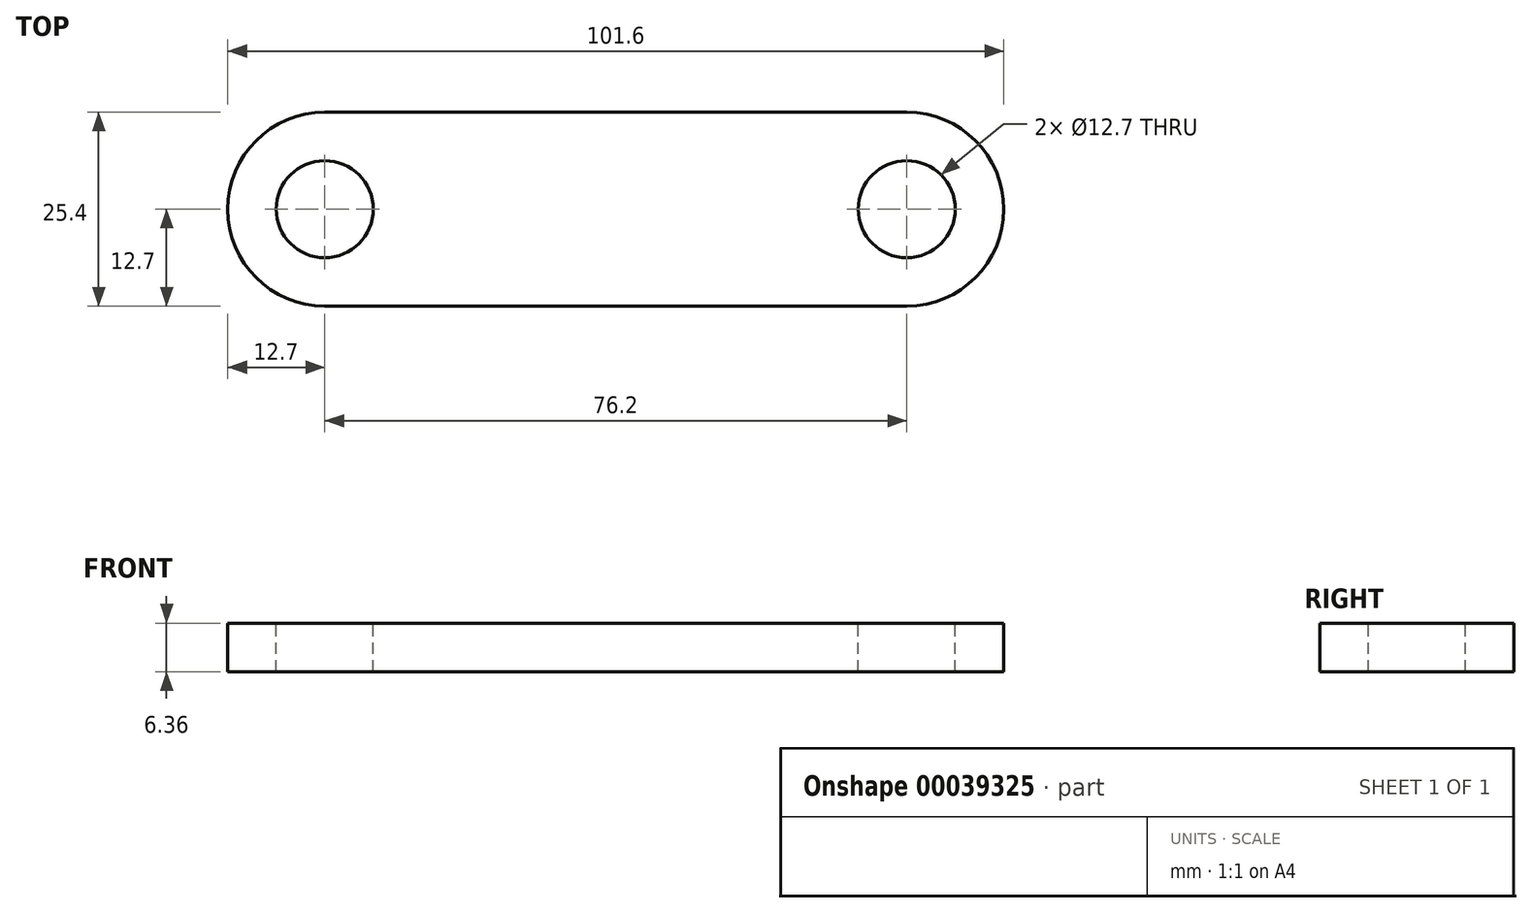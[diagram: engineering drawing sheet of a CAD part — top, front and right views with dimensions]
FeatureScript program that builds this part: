
annotation { "Feature Type Name" : "Feature", "Feature Type Description" : "" }
export const myFeature = defineFeature(function(context is Context, id is Id, definition is map)
    precondition{}
    {
        {
            var Q0;
            Q0=qCreatedBy(makeId("Top.planeOp"),FACE);
            var sketch = newSketch(context, id + "F0", { "sketchPlane" : qUnion([Q0])});
            skLineSegment(sketch, "E0.rect.bottom", {"start": v(50.8, 12.7) * mm, "end": v(-50.8, 12.7) * mm});
            skLineSegment(sketch, "E0.rect.top", {"start": v(50.8, -12.7) * mm, "end": v(-50.8, -12.7) * mm});
            skLineSegment(sketch, "E0.rect.left", {"start": v(50.8, 12.7) * mm, "end": v(50.8, -12.7) * mm});
            skLineSegment(sketch, "E0.rect.right", {"start": v(-50.8, 12.7) * mm, "end": v(-50.8, -12.7) * mm});
            skPoint(sketch, "E0.rect.middle", {"position": v(0, 0) * mm});
            skSolve(sketch);
        }
        {
            var Q0;
            Q0=makeQuery(id+"F0.imprint","IMPRINT",FACE,{"disambiguationData":[TD([[makeQuery(id+"F0.imprint","IMPRINT",EDGE,{"derivedFrom":sQuery(id+"F0.wireOp",EDGE,"E0.rect.bottom")}),1.0]])]});
            extrude(context, id + "F1", {"entities" : qUnion([Q0]), "depth" : 3.17 * mm, "hasSecondDirection" : true, "secondDirectionOppositeDirection" : true, "secondDirectionDepth" : 3.17 * mm});
        }
        {
            var Q0;
            Q0=makeQuery(id+"F1.opExtrude","CAP_FACE",FACE,{"disambiguationData":[OSD([sQuery(id+"F0.wireOp",EDGE,"E0.rect.bottom"),sQuery(id+"F0.wireOp",EDGE,"E0.rect.top"),sQuery(id+"F0.wireOp",EDGE,"E0.rect.left"),sQuery(id+"F0.wireOp",EDGE,"E0.rect.right")])],"isStart":false});
            var sketch = newSketch(context, id + "F2", { "sketchPlane" : qUnion([Q0])});
            skCircle(sketch, "E1", {"center": v(38.1, 0) * mm, "radius": 6.35 * mm});
            skLineSegment(sketch, "E2", {"start": v(0, 12.7) * mm, "end": v(0, -12.7) * mm, "construction": true});
            skCircle(sketch, "E3.MirrorC", {"center": v(-38.1, 0) * mm, "radius": 6.35 * mm});
            skSolve(sketch);
        }
        {
            var Q0;
            Q0 = qSketchRegion(id + "F2", true);
            extrude(context, id + "F3", {"entities" : qUnion([Q0]), "operationType" : NewBodyOperationType.REMOVE, "endBound" : BoundingType.THROUGH_ALL, "oppositeDirection" : true, "depth" : 25.4 * mm});
        }
        {
            var Q0;
            Q0 = qSketchRegion(id + "F2", true);
            extrude(context, id + "F4", {"entities" : qUnion([Q0]), "operationType" : NewBodyOperationType.REMOVE, "endBound" : BoundingType.THROUGH_ALL, "oppositeDirection" : true, "depth" : 25.4 * mm});
        }
        {
            var Q0;
            Q0=makeQuery(id+"F1.opExtrude","SWEPT_EDGE",EDGE,{"disambiguationData":[OSD([sQuery(id+"F0.wireOp",EDGE,"E0.rect.top"),sQuery(id+"F0.wireOp",EDGE,"E0.rect.left")])]});
            var Q1;
            Q1=makeQuery(id+"F1.opExtrude","SWEPT_EDGE",EDGE,{"disambiguationData":[OSD([sQuery(id+"F0.wireOp",EDGE,"E0.rect.top"),sQuery(id+"F0.wireOp",EDGE,"E0.rect.right")])]});
            var Q2;
            Q2=makeQuery(id+"F1.opExtrude","SWEPT_EDGE",EDGE,{"disambiguationData":[OSD([sQuery(id+"F0.wireOp",EDGE,"E0.rect.bottom"),sQuery(id+"F0.wireOp",EDGE,"E0.rect.left")])]});
            var Q3;
            Q3=makeQuery(id+"F1.opExtrude","SWEPT_EDGE",EDGE,{"disambiguationData":[OSD([sQuery(id+"F0.wireOp",EDGE,"E0.rect.bottom"),sQuery(id+"F0.wireOp",EDGE,"E0.rect.right")])]});
            fillet(context, id + "F5", {"entities" : qUnion([Q0, Q1, Q2, Q3]), "radius" : 12.7 * mm, "tangentPropagation" : true, "allowEdgeOverflow" : false});
        }
    });
